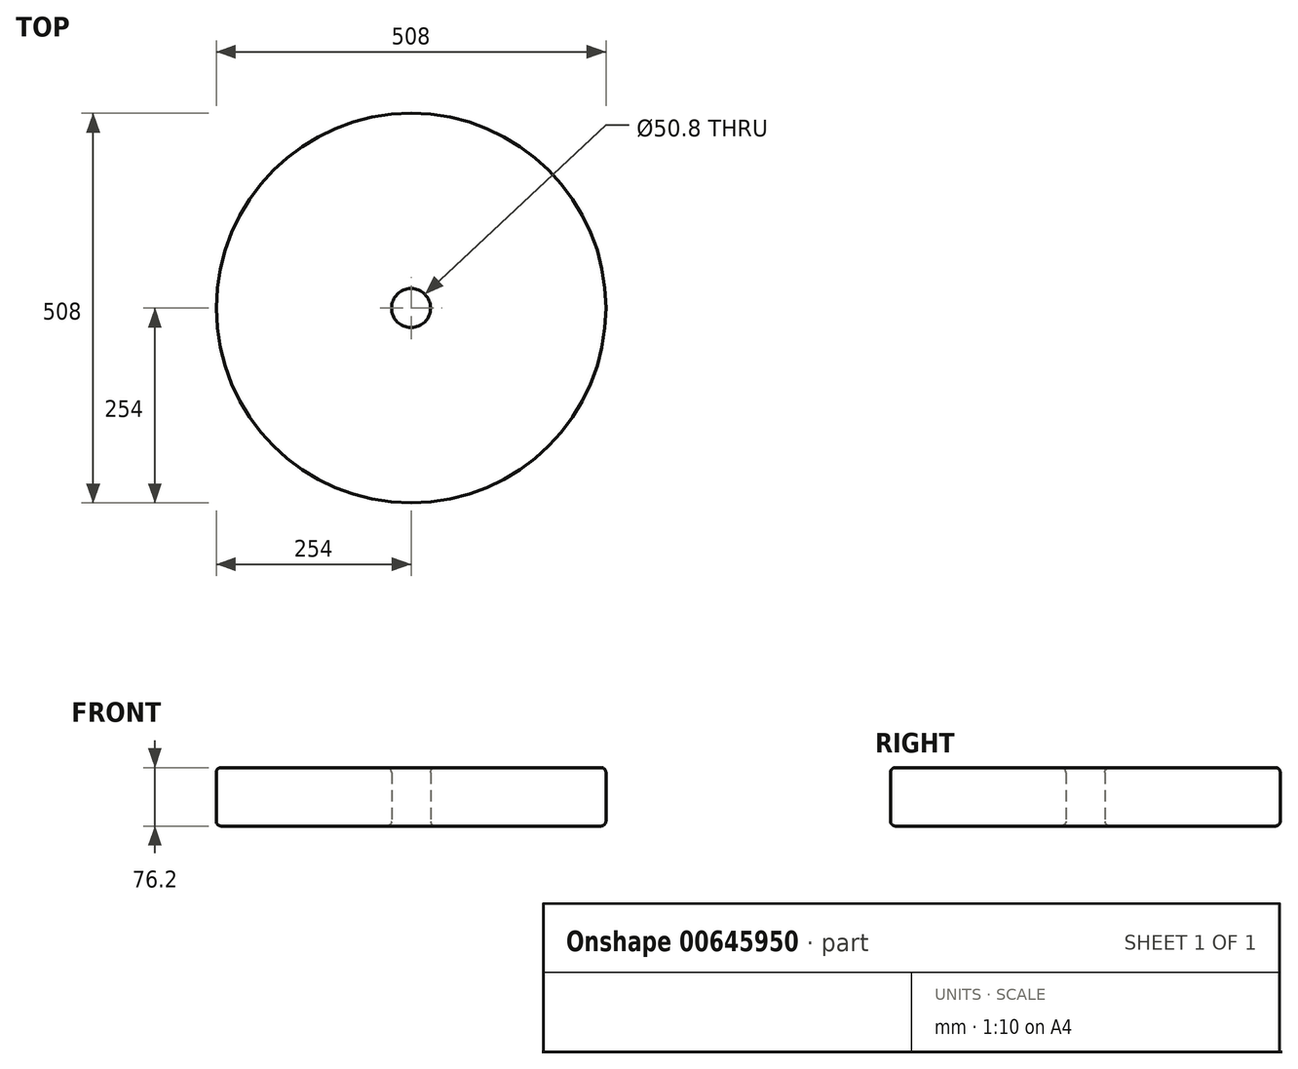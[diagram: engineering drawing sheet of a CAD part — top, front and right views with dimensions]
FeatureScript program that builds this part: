
annotation { "Feature Type Name" : "Feature", "Feature Type Description" : "" }
export const myFeature = defineFeature(function(context is Context, id is Id, definition is map)
    precondition{}
    {
        {
            var Q0;
            Q0=qCreatedBy(makeId("Front.planeOp"),FACE);
            var sketch = newSketch(context, id + "F0", { "sketchPlane" : qUnion([Q0])});
            skLineSegment(sketch, "E0", {"start": v(25.4, 76.2) * mm, "end": v(254, 76.2) * mm});
            skLineSegment(sketch, "E1", {"start": v(254, 0) * mm, "end": v(254, 76.2) * mm});
            skLineSegment(sketch, "E2", {"start": v(254, 0) * mm, "end": v(25.4, 0) * mm});
            skLineSegment(sketch, "E3", {"start": v(25.4, 76.2) * mm, "end": v(25.4, 0) * mm});
            skLineSegment(sketch, "E4", {"start": v(0, 0) * mm, "end": v(0, 160.66) * mm, "construction": true});
            skSolve(sketch);
        }
        {
            var Q0;
            Q0 = qSketchRegion(id + "F0", true);
            var Q1;
            Q1 = qConstructionFilter(qBodyType(qCreatedBy(id + "F0" ,EDGE), BodyType.WIRE), ConstructionObject.NO);
            var Q2;
            Q2=sQuery(id+"F0.wireOp",EDGE,"E4");
            revolve(context, id + "F1", {"entities" : qUnion([Q0]), "surfaceEntities" : qUnion([Q1]), "axis" : qUnion([Q2]), "revolveType" : RevolveType.FULL});
        }
        {
            var Q0;
            Q0=makeQuery(id+"F1.opRevolve","SWEPT_EDGE",EDGE,{"disambiguationData":[OSD([sQuery(id+"F0.wireOp",EDGE,"E0"),sQuery(id+"F0.wireOp",EDGE,"E1")])]});
            var Q1;
            Q1=makeQuery(id+"F1.opRevolve","SWEPT_EDGE",EDGE,{"disambiguationData":[OSD([sQuery(id+"F0.wireOp",EDGE,"E1"),sQuery(id+"F0.wireOp",EDGE,"E2")])]});
            var Q2;
            Q2=makeQuery(id+"F1.opRevolve","SWEPT_EDGE",EDGE,{"disambiguationData":[OSD([sQuery(id+"F0.wireOp",EDGE,"E0"),sQuery(id+"F0.wireOp",EDGE,"E3")])]});
            var Q3;
            Q3=makeQuery(id+"F1.opRevolve","SWEPT_EDGE",EDGE,{"disambiguationData":[OSD([sQuery(id+"F0.wireOp",EDGE,"E2"),sQuery(id+"F0.wireOp",EDGE,"E3")])]});
            fillet(context, id + "F2", {"entities" : qUnion([Q0, Q1, Q2, Q3]), "radius" : 6.35 * mm, "tangentPropagation" : true, "allowEdgeOverflow" : false});
        }
    });
